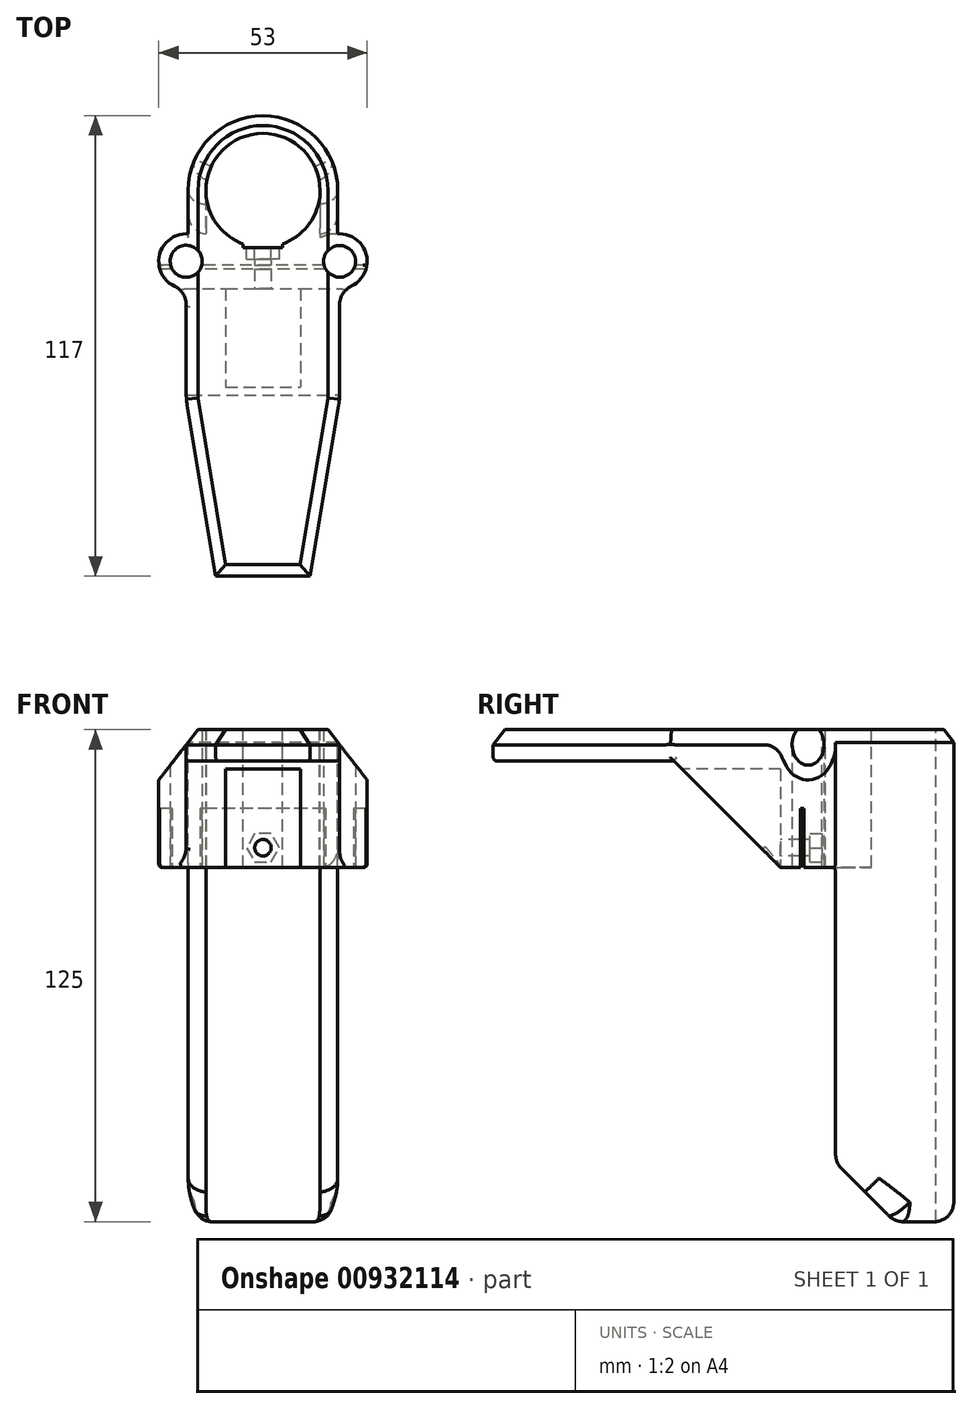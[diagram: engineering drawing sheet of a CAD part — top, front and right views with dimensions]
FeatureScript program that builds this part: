
annotation { "Feature Type Name" : "Feature", "Feature Type Description" : "" }
export const myFeature = defineFeature(function(context is Context, id is Id, definition is map)
    precondition{}
    {
        {
            var Q0;
            Q0=qCreatedBy(makeId("Top.planeOp"),FACE);
            var sketch = newSketch(context, id + "F0", { "sketchPlane" : qUnion([Q0])});
            skCircle(sketch, "E0", {"center": v(-19.5, 0) * mm, "radius": 4.08 * mm});
            skCircle(sketch, "E1", {"center": v(19.5, 0) * mm, "radius": 4.08 * mm});
            skLineSegment(sketch, "E2", {"start": v(0, 0) * mm, "end": v(-19.5, 0) * mm, "construction": true});
            skLineSegment(sketch, "E3", {"start": v(0, 0) * mm, "end": v(19.5, 0) * mm, "construction": true});
            skArc(sketch, "E4", {"start": v(-19.5, 7) * mm, "mid": v(-26.5, 0) * mm, "end": v(-19.5, -7) * mm});
            skArc(sketch, "E5", {"start": v(19.5, -7) * mm, "mid": v(26.5, 0) * mm, "end": v(19.5, 7) * mm});
            skLineSegment(sketch, "E6", {"start": v(-19.5, 7) * mm, "end": v(-19.5, 16.05) * mm});
            skLineSegment(sketch, "E7", {"start": v(-19.5, 16.05) * mm, "end": v(0, 16.05) * mm});
            skLineSegment(sketch, "E8.MirrorCS", {"start": v(19.5, 16.05) * mm, "end": v(0, 16.05) * mm});
            skLineSegment(sketch, "E9.MirrorCS", {"start": v(19.5, 7) * mm, "end": v(19.5, 16.05) * mm});
            skLineSegment(sketch, "E10", {"start": v(-19.5, 7) * mm, "end": v(-19.5, 0) * mm, "construction": true});
            skLineSegment(sketch, "E11", {"start": v(0, 16.05) * mm, "end": v(0, 16.05) * mm});
            skLineSegment(sketch, "E12", {"start": v(-19.5, -7) * mm, "end": v(-19.5, -35) * mm});
            skLineSegment(sketch, "E13", {"start": v(-19.5, -35) * mm, "end": v(-12, -80) * mm});
            skLineSegment(sketch, "E14", {"start": v(-12, -80) * mm, "end": v(0, -80) * mm});
            skLineSegment(sketch, "E15.MirrorCS", {"start": v(19.5, -7) * mm, "end": v(19.5, -35) * mm});
            skLineSegment(sketch, "E16.MirrorCS", {"start": v(12, -80) * mm, "end": v(0, -80) * mm});
            skLineSegment(sketch, "E17.MirrorCS", {"start": v(19.5, -35) * mm, "end": v(12, -80) * mm});
            skSolve(sketch);
        }
        {
            var Q0;
            Q0=makeQuery(id+"F0.imprint","IMPRINT",FACE,{"disambiguationData":[TD([[makeQuery(id+"F0.imprint","IMPRINT",EDGE,{"derivedFrom":sQuery(id+"F0.wireOp",EDGE,"E0")}),-1.0]])]});
            extrude(context, id + "F1", {"entities" : qUnion([Q0]), "depth" : 35 * mm, "offsetDistance" : 25 * mm});
        }
        {
            var Q0;
            Q0=makeQuery(id+"F1.opExtrude","SWEPT_FACE",FACE,{"disambiguationData":[OSD([sQuery(id+"F0.wireOp",EDGE,"E15.MirrorCS")])]});
            var sketch = newSketch(context, id + "F2", { "sketchPlane" : qUnion([Q0])});
            skLineSegment(sketch, "E18", {"start": v(-82.24, 27) * mm, "end": v(-34, 27) * mm});
            skLineSegment(sketch, "E19", {"start": v(-34, 27) * mm, "end": v(-7, 0) * mm});
            skLineSegment(sketch, "E20", {"start": v(-7, 0) * mm, "end": v(-7, 0) * mm});
            skLineSegment(sketch, "E21", {"start": v(-7, 0) * mm, "end": v(-7, -26.34) * mm});
            skLineSegment(sketch, "E22", {"start": v(-7, -26.34) * mm, "end": v(-82.24, -26.34) * mm});
            skLineSegment(sketch, "E23", {"start": v(-82.24, 27) * mm, "end": v(-82.24, -26.34) * mm});
            skSolve(sketch);
        }
        {
            var Q0;
            Q0=makeQuery(id+"F2.imprint","IMPRINT",FACE,{"disambiguationData":[TD([[makeQuery(id+"F2.imprint","IMPRINT",EDGE,{"derivedFrom":sQuery(id+"F2.wireOp",EDGE,"E21")}),-1.0]])]});
            var Q1;
            {var subQ0=sQuery(id+"F2.wireOp",EDGE,"E19");Q1=makeQuery(id+"F2.imprint","IMPRINT",FACE,{"disambiguationData":[TD([[makeQuery(id+"F2.imprint","IMPRINT",EDGE,{"derivedFrom":subQ0}),-1.0]])]});}
            extrude(context, id + "F3", {"entities" : qUnion([Q0, Q1]), "operationType" : NewBodyOperationType.REMOVE, "endBound" : BoundingType.THROUGH_ALL, "oppositeDirection" : true, "depth" : 25 * mm, "offsetDistance" : 25 * mm});
        }
        {
            var Q0;
            Q0=makeQuery(id+"F1.opExtrude","CAP_EDGE",EDGE,{"disambiguationData":[OSD([sQuery(id+"F0.wireOp",EDGE,"E13")])],"isStart":false});
            var Q1;
            Q1=makeQuery(id+"F1.opExtrude","CAP_EDGE",EDGE,{"disambiguationData":[OSD([sQuery(id+"F0.wireOp",EDGE,"E12")])],"isStart":false});
            var Q2;
            Q2=makeQuery(id+"F1.opExtrude","CAP_EDGE",EDGE,{"disambiguationData":[OSD([sQuery(id+"F0.wireOp",EDGE,"E15.MirrorCS")])],"isStart":false});
            var Q3;
            Q3=makeQuery(id+"F1.opExtrude","CAP_EDGE",EDGE,{"disambiguationData":[OSD([sQuery(id+"F0.wireOp",EDGE,"E9.MirrorCS")])],"isStart":false});
            var Q4;
            Q4=makeQuery(id+"F1.opExtrude","CAP_EDGE",EDGE,{"disambiguationData":[OSD([sQuery(id+"F0.wireOp",EDGE,"E6")])],"isStart":false});
            var Q5;
            Q5=makeQuery(id+"F1.opExtrude","CAP_EDGE",EDGE,{"disambiguationData":[OSD([sQuery(id+"F0.wireOp",EDGE,"E17.MirrorCS")])],"isStart":false});
            var Q6;
            Q6=makeQuery(id+"F1.opExtrude","CAP_EDGE",EDGE,{"disambiguationData":[OSD([sQuery(id+"F0.wireOp",EDGE,"E14"),sQuery(id+"F0.wireOp",EDGE,"E16.MirrorCS")])],"isStart":false});
            chamfer(context, id + "F4", {"entities" : qUnion([Q0, Q1, Q2, Q3, Q4, Q5, Q6]), "chamferType" : ChamferType.OFFSET_ANGLE, "width" : 3 * mm, "oppositeDirection" : false, "angle" : 52 * degree, "tangentPropagation" : true});
        }
        {
            var Q0;
            Q0=makeQuery(id+"F1.opExtrude","SWEPT_FACE",FACE,{"disambiguationData":[OSD([sQuery(id+"F0.wireOp",EDGE,"E14"),sQuery(id+"F0.wireOp",EDGE,"E16.MirrorCS")])]});
            var sketch = newSketch(context, id + "F5", { "sketchPlane" : qUnion([Q0])});
            skLineSegment(sketch, "E24", {"start": v(-16.5, 35) * mm, "end": v(-35.5, 10.68) * mm});
            skLineSegment(sketch, "E25", {"start": v(-35.5, 10.68) * mm, "end": v(-35.5, 37.22) * mm});
            skLineSegment(sketch, "E26", {"start": v(-35.5, 37.22) * mm, "end": v(0, 37.22) * mm});
            skLineSegment(sketch, "E27", {"start": v(0, 37.22) * mm, "end": v(0, 35) * mm});
            skLineSegment(sketch, "E28", {"start": v(0, 35) * mm, "end": v(-16.5, 35) * mm});
            skLineSegment(sketch, "E29.MirrorCS", {"start": v(0, 35) * mm, "end": v(16.5, 35) * mm});
            skLineSegment(sketch, "E30.MirrorCS", {"start": v(35.5, 37.22) * mm, "end": v(0, 37.22) * mm});
            skLineSegment(sketch, "E31.MirrorCS", {"start": v(35.5, 10.68) * mm, "end": v(35.5, 37.22) * mm});
            skLineSegment(sketch, "E32.MirrorCS", {"start": v(16.5, 35) * mm, "end": v(35.5, 10.68) * mm});
            skSolve(sketch);
        }
        {
            var Q0;
            Q0 = qSketchRegion(id + "F5", true);
            extrude(context, id + "F6", {"entities" : qUnion([Q0]), "operationType" : NewBodyOperationType.REMOVE, "endBound" : BoundingType.THROUGH_ALL, "oppositeDirection" : true, "depth" : 25 * mm, "offsetDistance" : 25 * mm});
        }
        {
            var Q0;
            Q0=makeQuery(id+"F1.opExtrude","CAP_FACE",FACE,{"disambiguationData":[OSD([sQuery(id+"F0.wireOp",EDGE,"E0"),sQuery(id+"F0.wireOp",EDGE,"E1"),sQuery(id+"F0.wireOp",EDGE,"E4"),sQuery(id+"F0.wireOp",EDGE,"E5"),sQuery(id+"F0.wireOp",EDGE,"E6"),sQuery(id+"F0.wireOp",EDGE,"E7"),sQuery(id+"F0.wireOp",EDGE,"E8.MirrorCS"),sQuery(id+"F0.wireOp",EDGE,"E9.MirrorCS"),sQuery(id+"F0.wireOp",EDGE,"4d2fa844-fc57-4d47-8dba-1bd83d5faa9b2.MirrorC"),sQuery(id+"F0.wireOp",EDGE,"E12"),sQuery(id+"F0.wireOp",EDGE,"E13"),sQuery(id+"F0.wireOp",EDGE,"E14"),sQuery(id+"F0.wireOp",EDGE,"E15.MirrorCS"),sQuery(id+"F0.wireOp",EDGE,"E16.MirrorCS"),sQuery(id+"F0.wireOp",EDGE,"E17.MirrorCS")])],"isStart":true});
            var sketch = newSketch(context, id + "F7", { "sketchPlane" : qUnion([Q0])});
            skLineSegment(sketch, "E33.bottom", {"start": v(96.32, 1) * mm, "end": v(-96.32, 1) * mm});
            skLineSegment(sketch, "E33.top", {"start": v(96.32, 2) * mm, "end": v(-96.32, 2) * mm});
            skLineSegment(sketch, "E33.left", {"start": v(96.32, 1) * mm, "end": v(96.32, 2) * mm});
            skLineSegment(sketch, "E33.right", {"start": v(-96.32, 1) * mm, "end": v(-96.32, 2) * mm});
            skPoint(sketch, "E33.middle", {"position": v(0, 1.5) * mm});
            skSolve(sketch);
        }
        {
            var Q0;
            Q0 = qSketchRegion(id + "F7", true);
            extrude(context, id + "F8", {"entities" : qUnion([Q0]), "operationType" : NewBodyOperationType.REMOVE, "oppositeDirection" : true, "depth" : 15 * mm, "offsetDistance" : 25 * mm});
        }
        {
            var Q0;
            {var subQ0=sQuery(id+"F0.wireOp",EDGE,"E4");var subQ1=sQuery(id+"F0.wireOp",EDGE,"E1");var subQ2=sQuery(id+"F0.wireOp",EDGE,"E15.MirrorCS");var subQ3=sQuery(id+"F0.wireOp",EDGE,"E5");var subQ4=sQuery(id+"F0.wireOp",EDGE,"E0");var subQ5=sQuery(id+"F0.wireOp",EDGE,"E12");Q0=makeQuery(id+"F8.boolean.opBoolean","SPLIT",FACE,{"disambiguationData":[TD([makeQuery(id+"F1.opExtrude","SWEPT_FACE",FACE,{"disambiguationData":[OSD([subQ5])]})])],"derivedFrom":makeQuery(id+"F1.opExtrude","CAP_FACE",FACE,{"disambiguationData":[OSD([subQ4,subQ1,subQ0,subQ3,sQuery(id+"F0.wireOp",EDGE,"E6"),sQuery(id+"F0.wireOp",EDGE,"E7"),sQuery(id+"F0.wireOp",EDGE,"E8.MirrorCS"),sQuery(id+"F0.wireOp",EDGE,"E9.MirrorCS"),sQuery(id+"F0.wireOp",EDGE,"4d2fa844-fc57-4d47-8dba-1bd83d5faa9b2.MirrorC"),subQ5,sQuery(id+"F0.wireOp",EDGE,"E13"),sQuery(id+"F0.wireOp",EDGE,"E14"),subQ2,sQuery(id+"F0.wireOp",EDGE,"E16.MirrorCS"),sQuery(id+"F0.wireOp",EDGE,"E17.MirrorCS")])],"isStart":true})});}
            var sketch = newSketch(context, id + "F9", { "sketchPlane" : qUnion([Q0])});
            skLineSegment(sketch, "E34.bottom", {"start": v(-3.75, 7) * mm, "end": v(3.75, 7) * mm});
            skLineSegment(sketch, "E34.top", {"start": v(-3.75, 17) * mm, "end": v(3.75, 17) * mm});
            skLineSegment(sketch, "E34.left", {"start": v(-3.75, 7) * mm, "end": v(-3.75, 17) * mm});
            skLineSegment(sketch, "E34.right", {"start": v(3.75, 7) * mm, "end": v(3.75, 17) * mm});
            skPoint(sketch, "E34.middle", {"position": v(0, 12) * mm});
            skPoint(sketch, "E34.middle.positionSnap0", {"position": v(0, 7) * mm});
            skPoint(sketch, "E34.centerSnap0", {"position": v(0, 7) * mm});
            skSolve(sketch);
        }
        {
            var Q0;
            Q0=makeQuery(id+"F9.imprint","IMPRINT",FACE,{"disambiguationData":[TD([[makeQuery(id+"F9.imprint","IMPRINT",EDGE,{"derivedFrom":sQuery(id+"F9.wireOp",EDGE,"E34.bottom")}),1.0]])]});
            extrude(context, id + "F10", {"entities" : qUnion([Q0]), "operationType" : NewBodyOperationType.REMOVE, "oppositeDirection" : true, "depth" : 10 * mm, "offsetDistance" : 25 * mm});
        }
        {
            var Q0;
            Q0=makeQuery(id+"F1.opExtrude","CAP_FACE",FACE,{"disambiguationData":[OSD([sQuery(id+"F0.wireOp",EDGE,"E0"),sQuery(id+"F0.wireOp",EDGE,"E1"),sQuery(id+"F0.wireOp",EDGE,"E4"),sQuery(id+"F0.wireOp",EDGE,"E5"),sQuery(id+"F0.wireOp",EDGE,"E6"),sQuery(id+"F0.wireOp",EDGE,"E7"),sQuery(id+"F0.wireOp",EDGE,"E8.MirrorCS"),sQuery(id+"F0.wireOp",EDGE,"E9.MirrorCS"),sQuery(id+"F0.wireOp",EDGE,"E12"),sQuery(id+"F0.wireOp",EDGE,"E13"),sQuery(id+"F0.wireOp",EDGE,"E14"),sQuery(id+"F0.wireOp",EDGE,"E15.MirrorCS"),sQuery(id+"F0.wireOp",EDGE,"E16.MirrorCS"),sQuery(id+"F0.wireOp",EDGE,"E17.MirrorCS")])],"isStart":false});
            var sketch = newSketch(context, id + "F11", { "sketchPlane" : qUnion([Q0])});
            skLineSegment(sketch, "E35.bottom", {"start": v(14.5, 16.05) * mm, "end": v(19.5, 16.05) * mm});
            skLineSegment(sketch, "E35.top", {"start": v(14.5, 7) * mm, "end": v(19.5, 7) * mm});
            skLineSegment(sketch, "E35.left", {"start": v(14.5, 16.05) * mm, "end": v(14.5, 7) * mm});
            skLineSegment(sketch, "E35.right", {"start": v(19.5, 16.05) * mm, "end": v(19.5, 7) * mm});
            skLineSegment(sketch, "E36.MirrorCS", {"start": v(-19.5, 16.05) * mm, "end": v(-19.5, 7) * mm});
            skLineSegment(sketch, "E37.MirrorCS", {"start": v(-14.5, 7) * mm, "end": v(-19.5, 7) * mm});
            skLineSegment(sketch, "E38.MirrorCS", {"start": v(-14.5, 16.05) * mm, "end": v(-14.5, 7) * mm});
            skLineSegment(sketch, "E39.MirrorCS", {"start": v(-14.5, 16.05) * mm, "end": v(-19.5, 16.05) * mm});
            skSolve(sketch);
        }
        {
            var Q0;
            Q0 = qSketchRegion(id + "F11", true);
            extrude(context, id + "F12", {"entities" : qUnion([Q0]), "operationType" : NewBodyOperationType.REMOVE, "endBound" : BoundingType.THROUGH_ALL, "oppositeDirection" : true, "depth" : 25 * mm, "offsetDistance" : 25 * mm});
        }
        {
            var Q0;
            Q0=makeQuery(id+"F10.boolean.opBoolean","COPY",FACE,{"derivedFrom":makeQuery(id+"F10.opExtrude","SWEPT_FACE",FACE,{"disambiguationData":[OSD([sQuery(id+"F9.wireOp",EDGE,"E34.bottom")])]})});
            var sketch = newSketch(context, id + "F13", { "sketchPlane" : qUnion([Q0])});
            skCircle(sketch, "E40", {"center": v(0, 5) * mm, "radius": 2.1 * mm});
            skSolve(sketch);
        }
        {
            var Q0;
            Q0 = qSketchRegion(id + "F13", true);
            extrude(context, id + "F14", {"entities" : qUnion([Q0]), "operationType" : NewBodyOperationType.REMOVE, "oppositeDirection" : true, "depth" : 25 * mm, "offsetDistance" : 25 * mm});
        }
        {
            var Q0;
            Q0=makeQuery(id+"F1.opExtrude","SWEPT_FACE",FACE,{"disambiguationData":[OSD([sQuery(id+"F0.wireOp",EDGE,"E7"),sQuery(id+"F0.wireOp",EDGE,"E8.MirrorCS")])]});
            var sketch = newSketch(context, id + "F15", { "sketchPlane" : qUnion([Q0])});
            skCircle(sketch, "E41.cCircle", {"center": v(0, 5) * mm, "radius": 3.6 * mm, "construction": true});
            skLineSegment(sketch, "E41.0", {"start": v(-4.16, 5) * mm, "end": v(-2.08, 8.6) * mm});
            skLineSegment(sketch, "E41.1", {"start": v(-2.08, 8.6) * mm, "end": v(2.08, 8.6) * mm});
            skLineSegment(sketch, "E41.2", {"start": v(2.08, 8.6) * mm, "end": v(4.16, 5) * mm});
            skLineSegment(sketch, "E41.3", {"start": v(4.16, 5) * mm, "end": v(2.08, 1.4) * mm});
            skLineSegment(sketch, "E41.4", {"start": v(2.08, 1.4) * mm, "end": v(-2.08, 1.4) * mm});
            skLineSegment(sketch, "E41.5", {"start": v(-2.08, 1.4) * mm, "end": v(-4.16, 5) * mm});
            skPoint(sketch, "E41.0.midPoint", {"position": v(-3.12, 6.8) * mm});
            skLineSegment(sketch, "E42", {"start": v(0, 5) * mm, "end": v(0, 0) * mm, "construction": true});
            skSolve(sketch);
        }
        {
            var Q0;
            Q0=makeQuery(id+"F15.imprint","IMPRINT",FACE,{"disambiguationData":[TD([[makeQuery(id+"F15.imprint","IMPRINT",EDGE,{"derivedFrom":sQuery(id+"F15.wireOp",EDGE,"E41.0")}),-1.0]])]});
            extrude(context, id + "F16", {"entities" : qUnion([Q0]), "operationType" : NewBodyOperationType.REMOVE, "oppositeDirection" : true, "depth" : 6 * mm, "offsetDistance" : 25 * mm});
        }
        {
            var Q0;
            {var subQ0=sQuery(id+"F0.wireOp",EDGE,"E4");var subQ1=sQuery(id+"F0.wireOp",EDGE,"E1");var subQ2=sQuery(id+"F0.wireOp",EDGE,"E5");var subQ3=sQuery(id+"F0.wireOp",EDGE,"E0");var subQ4=sQuery(id+"F0.wireOp",EDGE,"E12");var subQ5=sQuery(id+"F0.wireOp",EDGE,"E15.MirrorCS");Q0=makeQuery(id+"F8.boolean.opBoolean","SPLIT",FACE,{"disambiguationData":[TD([makeQuery(id+"F1.opExtrude","SWEPT_FACE",FACE,{"disambiguationData":[OSD([subQ4])]})])],"derivedFrom":makeQuery(id+"F1.opExtrude","CAP_FACE",FACE,{"disambiguationData":[OSD([subQ3,subQ1,subQ0,subQ2,sQuery(id+"F0.wireOp",EDGE,"E6"),sQuery(id+"F0.wireOp",EDGE,"E7"),sQuery(id+"F0.wireOp",EDGE,"E8.MirrorCS"),sQuery(id+"F0.wireOp",EDGE,"E9.MirrorCS"),subQ4,sQuery(id+"F0.wireOp",EDGE,"E13"),sQuery(id+"F0.wireOp",EDGE,"E14"),subQ5,sQuery(id+"F0.wireOp",EDGE,"E16.MirrorCS"),sQuery(id+"F0.wireOp",EDGE,"E17.MirrorCS")])],"isStart":true})});}
            var sketch = newSketch(context, id + "F17", { "sketchPlane" : qUnion([Q0])});
            skLineSegment(sketch, "E43.bottom", {"start": v(-9.5, 7) * mm, "end": v(9.5, 7) * mm});
            skLineSegment(sketch, "E43.top", {"start": v(-9.5, 43.79) * mm, "end": v(9.5, 43.79) * mm});
            skLineSegment(sketch, "E43.left", {"start": v(-9.5, 7) * mm, "end": v(-9.5, 43.79) * mm});
            skLineSegment(sketch, "E43.right", {"start": v(9.5, 7) * mm, "end": v(9.5, 43.79) * mm});
            skSolve(sketch);
        }
        {
            var Q0;
            Q0=makeQuery(id+"F17.imprint","IMPRINT",FACE,{"disambiguationData":[TD([[makeQuery(id+"F17.imprint","IMPRINT",EDGE,{"derivedFrom":sQuery(id+"F17.wireOp",EDGE,"E43.top")}),-1.0]])]});
            extrude(context, id + "F18", {"entities" : qUnion([Q0]), "operationType" : NewBodyOperationType.REMOVE, "oppositeDirection" : true, "depth" : 25 * mm, "offsetDistance" : 25 * mm});
        }
        {
            var Q0;
            Q0=makeQuery(id+"F1.opExtrude","SWEPT_EDGE",EDGE,{"disambiguationData":[OSD([sQuery(id+"F0.wireOp",EDGE,"E4"),sQuery(id+"F0.wireOp",EDGE,"E12")])]});
            var Q1;
            Q1=makeQuery(id+"F1.opExtrude","SWEPT_EDGE",EDGE,{"disambiguationData":[OSD([sQuery(id+"F0.wireOp",EDGE,"E5"),sQuery(id+"F0.wireOp",EDGE,"E15.MirrorCS")])]});
            fillet(context, id + "F19", {"entities" : qUnion([Q0, Q1]), "radius" : 5 * mm, "tangentPropagation" : true, "allowEdgeOverflow" : false});
        }
        {
            var Q0;
            Q0=makeQuery(id+"F1.opExtrude","SWEPT_EDGE",EDGE,{"disambiguationData":[OSD([sQuery(id+"F0.wireOp",EDGE,"E12"),sQuery(id+"F0.wireOp",EDGE,"E13")])]});
            var Q1;
            Q1=makeQuery(id+"F1.opExtrude","SWEPT_EDGE",EDGE,{"disambiguationData":[OSD([sQuery(id+"F0.wireOp",EDGE,"E15.MirrorCS"),sQuery(id+"F0.wireOp",EDGE,"E17.MirrorCS")])]});
            fillet(context, id + "F20", {"entities" : qUnion([Q0, Q1]), "radius" : 20 * mm, "tangentPropagation" : true, "allowEdgeOverflow" : false});
        }
        {
            var Q0;
            Q0=makeQuery(id+"F1.opExtrude","CAP_FACE",FACE,{"disambiguationData":[OSD([sQuery(id+"F0.wireOp",EDGE,"E0"),sQuery(id+"F0.wireOp",EDGE,"E1"),sQuery(id+"F0.wireOp",EDGE,"E4"),sQuery(id+"F0.wireOp",EDGE,"E5"),sQuery(id+"F0.wireOp",EDGE,"E6"),sQuery(id+"F0.wireOp",EDGE,"E7"),sQuery(id+"F0.wireOp",EDGE,"E8.MirrorCS"),sQuery(id+"F0.wireOp",EDGE,"E9.MirrorCS"),sQuery(id+"F0.wireOp",EDGE,"E12"),sQuery(id+"F0.wireOp",EDGE,"E13"),sQuery(id+"F0.wireOp",EDGE,"E14"),sQuery(id+"F0.wireOp",EDGE,"E15.MirrorCS"),sQuery(id+"F0.wireOp",EDGE,"E16.MirrorCS"),sQuery(id+"F0.wireOp",EDGE,"E17.MirrorCS")])],"isStart":false});
            var sketch = newSketch(context, id + "F21", { "sketchPlane" : qUnion([Q0])});
            skLineSegment(sketch, "E44", {"start": v(-14.5, 18) * mm, "end": v(-14.5, 18) * mm});
            skArc(sketch, "E45", {"start": v(19, 18) * mm, "mid": v(0, 37) * mm, "end": v(-19, 18) * mm});
            skLineSegment(sketch, "E46", {"start": v(-19, 18) * mm, "end": v(-19, 7) * mm});
            skLineSegment(sketch, "E47", {"start": v(-19, 7) * mm, "end": v(-14.5, 7) * mm});
            skLineSegment(sketch, "E48", {"start": v(-14.5, 7) * mm, "end": v(-14.5, 18) * mm});
            skArc(sketch, "E49", {"start": v(14.5, 18) * mm, "mid": v(0, 32.5) * mm, "end": v(-14.5, 18) * mm});
            skLineSegment(sketch, "E50.MirrorCS", {"start": v(19, 18) * mm, "end": v(19, 7) * mm});
            skLineSegment(sketch, "E51.MirrorCS", {"start": v(14.5, 7) * mm, "end": v(14.5, 18) * mm});
            skLineSegment(sketch, "E52", {"start": v(0, 18) * mm, "end": v(0, 0) * mm, "construction": true});
            skLineSegment(sketch, "E53", {"start": v(14.5, 7) * mm, "end": v(19, 7) * mm});
            skSolve(sketch);
        }
        {
            var Q0;
            Q0=makeQuery(id+"F21.imprint","IMPRINT",FACE,{"disambiguationData":[TD([[makeQuery(id+"F21.imprint","IMPRINT",EDGE,{"derivedFrom":sQuery(id+"F21.wireOp",EDGE,"E45")}),1.0]])]});
            extrude(context, id + "F22", {"entities" : qUnion([Q0]), "operationType" : NewBodyOperationType.ADD, "oppositeDirection" : true, "depth" : 125 * mm, "offsetDistance" : 25 * mm});
        }
        {
            var Q0;
            Q0=makeQuery(id+"F22.opExtrude","CAP_EDGE",EDGE,{"disambiguationData":[OSD([sQuery(id+"F21.wireOp",EDGE,"E46")])],"isStart":true});
            var Q1;
            Q1=makeQuery(id+"F22.opExtrude","CAP_EDGE",EDGE,{"disambiguationData":[OSD([sQuery(id+"F21.wireOp",EDGE,"E45")])],"isStart":true});
            var Q2;
            Q2=makeQuery(id+"F22.opExtrude","CAP_EDGE",EDGE,{"disambiguationData":[OSD([sQuery(id+"F21.wireOp",EDGE,"E50.MirrorCS")])],"isStart":true});
            chamfer(context, id + "F23", {"entities" : qUnion([Q0, Q1, Q2]), "chamferType" : ChamferType.OFFSET_ANGLE, "width" : 2.5 * mm, "oppositeDirection" : false, "angle" : 52 * degree, "tangentPropagation" : true});
        }
        {
            var Q0;
            Q0=makeQuery(id+"F22.boolean.opBoolean","MERGE",FACE,{"derivedFrom":[makeQuery(id+"F1.opExtrude","CAP_FACE",FACE,{"disambiguationData":[OSD([sQuery(id+"F0.wireOp",EDGE,"E0"),sQuery(id+"F0.wireOp",EDGE,"E1"),sQuery(id+"F0.wireOp",EDGE,"E4"),sQuery(id+"F0.wireOp",EDGE,"E5"),sQuery(id+"F0.wireOp",EDGE,"E6"),sQuery(id+"F0.wireOp",EDGE,"E7"),sQuery(id+"F0.wireOp",EDGE,"E8.MirrorCS"),sQuery(id+"F0.wireOp",EDGE,"E9.MirrorCS"),sQuery(id+"F0.wireOp",EDGE,"E12"),sQuery(id+"F0.wireOp",EDGE,"E13"),sQuery(id+"F0.wireOp",EDGE,"E14"),sQuery(id+"F0.wireOp",EDGE,"E15.MirrorCS"),sQuery(id+"F0.wireOp",EDGE,"E16.MirrorCS"),sQuery(id+"F0.wireOp",EDGE,"E17.MirrorCS")])],"isStart":false}),makeQuery(id+"F22.opExtrude","CAP_FACE",FACE,{"disambiguationData":[OSD([sQuery(id+"F21.wireOp",EDGE,"E45"),sQuery(id+"F21.wireOp",EDGE,"E46"),sQuery(id+"F21.wireOp",EDGE,"E47"),sQuery(id+"F21.wireOp",EDGE,"E48"),sQuery(id+"F21.wireOp",EDGE,"E49"),sQuery(id+"F21.wireOp",EDGE,"E50.MirrorCS"),sQuery(id+"F21.wireOp",EDGE,"E51.MirrorCS"),sQuery(id+"F21.wireOp",EDGE,"E53")])],"isStart":true})]});
            var sketch = newSketch(context, id + "F24", { "sketchPlane" : qUnion([Q0])});
            skArc(sketch, "E54", {"start": v(5, 4.39) * mm, "mid": v(0, 32.5) * mm, "end": v(-5, 4.39) * mm});
            skLineSegment(sketch, "E55.bottom", {"start": v(-5, 3.5) * mm, "end": v(5, 3.5) * mm});
            skLineSegment(sketch, "E55.left", {"start": v(-5, 3.5) * mm, "end": v(-5, 4.39) * mm});
            skLineSegment(sketch, "E55.right", {"start": v(5, 3.5) * mm, "end": v(5, 4.39) * mm});
            skPoint(sketch, "E55.middle", {"position": v(0, 5.46) * mm});
            skPoint(sketch, "E55.top.end.orphan", {"position": v(5, 7.42) * mm});
            skPoint(sketch, "E55.top.start.orphan", {"position": v(-5, 7.42) * mm});
            skSolve(sketch);
        }
        {
            var Q0;
            Q0 = qSketchRegion(id + "F24", true);
            extrude(context, id + "F25", {"entities" : qUnion([Q0]), "operationType" : NewBodyOperationType.REMOVE, "endBound" : BoundingType.THROUGH_ALL, "oppositeDirection" : true, "depth" : 25 * mm, "offsetDistance" : 25 * mm});
        }
        {
            var Q0;
            Q0=makeQuery(id+"F3.boolean.opBoolean","INTERSECT",EDGE,{"derivedFrom":[makeQuery(id+"F1.opExtrude","SWEPT_FACE",FACE,{"disambiguationData":[OSD([sQuery(id+"F0.wireOp",EDGE,"E17.MirrorCS")])]}),makeQuery(id+"F3.opExtrude","SWEPT_FACE",FACE,{"disambiguationData":[OSD([sQuery(id+"F2.wireOp",EDGE,"E18")])]})]});
            var Q1;
            Q1=makeQuery(id+"F3.boolean.opBoolean","INTERSECT",EDGE,{"derivedFrom":[makeQuery(id+"F1.opExtrude","SWEPT_FACE",FACE,{"disambiguationData":[OSD([sQuery(id+"F0.wireOp",EDGE,"E14"),sQuery(id+"F0.wireOp",EDGE,"E16.MirrorCS")])]}),makeQuery(id+"F3.opExtrude","SWEPT_FACE",FACE,{"disambiguationData":[OSD([sQuery(id+"F2.wireOp",EDGE,"E18")])]})]});
            var Q2;
            Q2=makeQuery(id+"F3.boolean.opBoolean","INTERSECT",EDGE,{"derivedFrom":[makeQuery(id+"F1.opExtrude","SWEPT_FACE",FACE,{"disambiguationData":[OSD([sQuery(id+"F0.wireOp",EDGE,"E13")])]}),makeQuery(id+"F3.opExtrude","SWEPT_FACE",FACE,{"disambiguationData":[OSD([sQuery(id+"F2.wireOp",EDGE,"E18")])]})]});
            var Q3;
            Q3=makeQuery(id+"F3.boolean.opBoolean","INTERSECT",EDGE,{"derivedFrom":[makeQuery(id+"F1.opExtrude","SWEPT_FACE",FACE,{"disambiguationData":[OSD([sQuery(id+"F0.wireOp",EDGE,"E12")])]}),makeQuery(id+"F3.opExtrude","SWEPT_FACE",FACE,{"disambiguationData":[OSD([sQuery(id+"F2.wireOp",EDGE,"E19")])]})]});
            var Q4;
            Q4=makeQuery(id+"F3.boolean.opBoolean","COPY",EDGE,{"derivedFrom":makeQuery(id+"F3.opExtrude","CAP_EDGE",EDGE,{"disambiguationData":[OSD([sQuery(id+"F2.wireOp",EDGE,"E19")])],"isStart":true})});
            var Q5;
            {var subQ0=sQuery(id+"F0.wireOp",EDGE,"E15.MirrorCS");var subQ1=sQuery(id+"F0.wireOp",EDGE,"E5");Q5=makeQuery(id+"F8.boolean.opBoolean","SPLIT",EDGE,{"disambiguationData":[TD([makeQuery(id+"F1.opExtrude","SWEPT_FACE",FACE,{"disambiguationData":[OSD([subQ0])]})])],"derivedFrom":makeQuery(id+"F1.opExtrude","CAP_EDGE",EDGE,{"disambiguationData":[OSD([subQ1])],"isStart":true})});}
            var Q6;
            {var subQ0=sQuery(id+"F0.wireOp",EDGE,"E9.MirrorCS");var subQ1=sQuery(id+"F0.wireOp",EDGE,"E5");Q6=makeQuery(id+"F8.boolean.opBoolean","SPLIT",EDGE,{"disambiguationData":[TD([makeQuery(id+"F1.opExtrude","SWEPT_FACE",FACE,{"disambiguationData":[OSD([subQ0])]})])],"derivedFrom":makeQuery(id+"F1.opExtrude","CAP_EDGE",EDGE,{"disambiguationData":[OSD([subQ1])],"isStart":true})});}
            var Q7;
            {var subQ0=sQuery(id+"F0.wireOp",EDGE,"E12");var subQ1=sQuery(id+"F0.wireOp",EDGE,"E4");Q7=makeQuery(id+"F8.boolean.opBoolean","SPLIT",EDGE,{"disambiguationData":[TD([makeQuery(id+"F1.opExtrude","SWEPT_FACE",FACE,{"disambiguationData":[OSD([subQ0])]})])],"derivedFrom":makeQuery(id+"F1.opExtrude","CAP_EDGE",EDGE,{"disambiguationData":[OSD([subQ1])],"isStart":true})});}
            var Q8;
            {var subQ0=sQuery(id+"F0.wireOp",EDGE,"E6");var subQ1=sQuery(id+"F0.wireOp",EDGE,"E4");Q8=makeQuery(id+"F8.boolean.opBoolean","SPLIT",EDGE,{"disambiguationData":[TD([makeQuery(id+"F1.opExtrude","SWEPT_FACE",FACE,{"disambiguationData":[OSD([subQ0])]})])],"derivedFrom":makeQuery(id+"F1.opExtrude","CAP_EDGE",EDGE,{"disambiguationData":[OSD([subQ1])],"isStart":true})});}
            fillet(context, id + "F26", {"entities" : qUnion([Q0, Q1, Q2, Q3, Q4, Q5, Q6, Q7, Q8]), "radius" : 1 * mm, "tangentPropagation" : true, "allowEdgeOverflow" : false});
        }
        {
            var Q0;
            Q0=makeQuery(id+"F22.opExtrude","CAP_EDGE",EDGE,{"disambiguationData":[OSD([sQuery(id+"F21.wireOp",EDGE,"E53")])],"isStart":false});
            var Q1;
            Q1=makeQuery(id+"F22.opExtrude","CAP_EDGE",EDGE,{"disambiguationData":[OSD([sQuery(id+"F21.wireOp",EDGE,"E47")])],"isStart":false});
            chamfer(context, id + "F27", {"entities" : qUnion([Q0, Q1]), "width" : 15 * mm, "tangentPropagation" : true});
        }
        {
            var Q0;
            {var subQ0=sQuery(id+"F21.wireOp",EDGE,"E53");Q0=makeQuery(id+"F27.opChamfer","BLEND_EDGE",EDGE,{"blendedFrom":[makeQuery(id+"F22.opExtrude","CAP_EDGE",EDGE,{"disambiguationData":[OSD([subQ0])],"isStart":false}),makeQuery(id+"F22.opExtrude","CAP_FACE",FACE,{"disambiguationData":[OSD([sQuery(id+"F21.wireOp",EDGE,"E45"),sQuery(id+"F21.wireOp",EDGE,"E46"),sQuery(id+"F21.wireOp",EDGE,"E47"),sQuery(id+"F21.wireOp",EDGE,"E48"),sQuery(id+"F21.wireOp",EDGE,"E49"),sQuery(id+"F21.wireOp",EDGE,"E50.MirrorCS"),sQuery(id+"F21.wireOp",EDGE,"E51.MirrorCS"),subQ0])],"isStart":false})],"blendedInto":[makeQuery(id+"F22.opExtrude","CAP_FACE",FACE,{"disambiguationData":[OSD([sQuery(id+"F21.wireOp",EDGE,"E45"),sQuery(id+"F21.wireOp",EDGE,"E46"),sQuery(id+"F21.wireOp",EDGE,"E47"),sQuery(id+"F21.wireOp",EDGE,"E48"),sQuery(id+"F21.wireOp",EDGE,"E49"),sQuery(id+"F21.wireOp",EDGE,"E50.MirrorCS"),sQuery(id+"F21.wireOp",EDGE,"E51.MirrorCS"),subQ0])],"isStart":false})]});}
            var Q1;
            {var subQ0=sQuery(id+"F21.wireOp",EDGE,"E47");Q1=makeQuery(id+"F27.opChamfer","BLEND_EDGE",EDGE,{"blendedFrom":[makeQuery(id+"F22.opExtrude","CAP_EDGE",EDGE,{"disambiguationData":[OSD([subQ0])],"isStart":false}),makeQuery(id+"F22.opExtrude","CAP_FACE",FACE,{"disambiguationData":[OSD([sQuery(id+"F21.wireOp",EDGE,"E45"),sQuery(id+"F21.wireOp",EDGE,"E46"),subQ0,sQuery(id+"F21.wireOp",EDGE,"E48"),sQuery(id+"F21.wireOp",EDGE,"E49"),sQuery(id+"F21.wireOp",EDGE,"E50.MirrorCS"),sQuery(id+"F21.wireOp",EDGE,"E51.MirrorCS"),sQuery(id+"F21.wireOp",EDGE,"E53")])],"isStart":false})],"blendedInto":[makeQuery(id+"F22.opExtrude","CAP_FACE",FACE,{"disambiguationData":[OSD([sQuery(id+"F21.wireOp",EDGE,"E45"),sQuery(id+"F21.wireOp",EDGE,"E46"),subQ0,sQuery(id+"F21.wireOp",EDGE,"E48"),sQuery(id+"F21.wireOp",EDGE,"E49"),sQuery(id+"F21.wireOp",EDGE,"E50.MirrorCS"),sQuery(id+"F21.wireOp",EDGE,"E51.MirrorCS"),sQuery(id+"F21.wireOp",EDGE,"E53")])],"isStart":false})]});}
            var Q2;
            {var subQ1=sQuery(id+"F21.wireOp",EDGE,"E53");var subQ2=sQuery(id+"F21.wireOp",EDGE,"E51.MirrorCS");Q2=makeQuery(id+"F27.opChamfer","BLEND_EDGE",EDGE,{"blendedFrom":[makeQuery(id+"F22.opExtrude","CAP_EDGE",EDGE,{"disambiguationData":[OSD([subQ1])],"isStart":false}),makeQuery(id+"F22.boolean.opBoolean","SPLIT",FACE,{"disambiguationData":[TD([makeQuery(id+"F22.opExtrude","SWEPT_FACE",FACE,{"disambiguationData":[OSD([subQ2])]})])],"derivedFrom":makeQuery(id+"F22.opExtrude","SWEPT_FACE",FACE,{"disambiguationData":[OSD([subQ1])]})})],"blendedInto":[makeQuery(id+"F22.boolean.opBoolean","SPLIT",FACE,{"disambiguationData":[TD([makeQuery(id+"F22.opExtrude","SWEPT_FACE",FACE,{"disambiguationData":[OSD([subQ2])]})])],"derivedFrom":makeQuery(id+"F22.opExtrude","SWEPT_FACE",FACE,{"disambiguationData":[OSD([subQ1])]})})]});}
            var Q3;
            {var subQ0=sQuery(id+"F21.wireOp",EDGE,"E48");var subQ1=sQuery(id+"F21.wireOp",EDGE,"E47");Q3=makeQuery(id+"F27.opChamfer","BLEND_EDGE",EDGE,{"blendedFrom":[makeQuery(id+"F22.opExtrude","CAP_EDGE",EDGE,{"disambiguationData":[OSD([subQ1])],"isStart":false}),makeQuery(id+"F22.boolean.opBoolean","SPLIT",FACE,{"disambiguationData":[TD([makeQuery(id+"F22.opExtrude","SWEPT_FACE",FACE,{"disambiguationData":[OSD([subQ0])]})])],"derivedFrom":makeQuery(id+"F22.opExtrude","SWEPT_FACE",FACE,{"disambiguationData":[OSD([subQ1])]})})],"blendedInto":[makeQuery(id+"F22.boolean.opBoolean","SPLIT",FACE,{"disambiguationData":[TD([makeQuery(id+"F22.opExtrude","SWEPT_FACE",FACE,{"disambiguationData":[OSD([subQ0])]})])],"derivedFrom":makeQuery(id+"F22.opExtrude","SWEPT_FACE",FACE,{"disambiguationData":[OSD([subQ1])]})})]});}
            fillet(context, id + "F28", {"entities" : qUnion([Q0, Q1, Q2, Q3]), "radius" : 5 * mm, "tangentPropagation" : true, "allowEdgeOverflow" : false});
        }
        {
            var Q0;
            {var subQ0=sQuery(id+"F0.wireOp",EDGE,"E9.MirrorCS");var subQ1=sQuery(id+"F0.wireOp",EDGE,"E8.MirrorCS");var subQ2=sQuery(id+"F0.wireOp",EDGE,"E7");var subQ3=sQuery(id+"F0.wireOp",EDGE,"E6");var subQ4=sQuery(id+"F0.wireOp",EDGE,"E5");var subQ5=sQuery(id+"F0.wireOp",EDGE,"E4");var subQ6=sQuery(id+"F0.wireOp",EDGE,"E1");var subQ7=sQuery(id+"F0.wireOp",EDGE,"E0");var subQ8=makeQuery(id+"F1.opExtrude","CAP_FACE",FACE,{"disambiguationData":[OSD([subQ7,subQ6,subQ5,subQ4,subQ3,subQ2,subQ1,subQ0,sQuery(id+"F0.wireOp",EDGE,"E12"),sQuery(id+"F0.wireOp",EDGE,"E13"),sQuery(id+"F0.wireOp",EDGE,"E14"),sQuery(id+"F0.wireOp",EDGE,"E15.MirrorCS"),sQuery(id+"F0.wireOp",EDGE,"E16.MirrorCS"),sQuery(id+"F0.wireOp",EDGE,"E17.MirrorCS")])],"isStart":true});Q0=makeQuery(id+"F22.boolean.opBoolean","SPLIT",EDGE,{"disambiguationData":[topologyDisambiguationEdgeConnected([makeQuery(id+"F22.opExtrude","SWEPT_FACE",FACE,{"disambiguationData":[OSD([sQuery(id+"F21.wireOp",EDGE,"E53")])]})])],"derivedFrom":makeQuery(id+"F12.boolean.opBoolean","INTERSECT",EDGE,{"derivedFrom":[makeQuery(id+"F8.boolean.opBoolean","SPLIT",FACE,{"disambiguationData":[TD([makeQuery(id+"F1.opExtrude","SWEPT_FACE",FACE,{"disambiguationData":[OSD([subQ3])]})])],"derivedFrom":subQ8}),makeQuery(id+"F12.opExtrude","SWEPT_FACE",FACE,{"disambiguationData":[OSD([sQuery(id+"F11.wireOp",EDGE,"E35.top")])]})]})});}
            var Q1;
            {var subQ0=sQuery(id+"F0.wireOp",EDGE,"E9.MirrorCS");var subQ1=sQuery(id+"F0.wireOp",EDGE,"E8.MirrorCS");var subQ2=sQuery(id+"F0.wireOp",EDGE,"E7");var subQ3=sQuery(id+"F0.wireOp",EDGE,"E6");var subQ4=sQuery(id+"F0.wireOp",EDGE,"E5");var subQ5=sQuery(id+"F0.wireOp",EDGE,"E4");var subQ6=sQuery(id+"F0.wireOp",EDGE,"E1");var subQ7=sQuery(id+"F0.wireOp",EDGE,"E0");var subQ8=makeQuery(id+"F1.opExtrude","CAP_FACE",FACE,{"disambiguationData":[OSD([subQ7,subQ6,subQ5,subQ4,subQ3,subQ2,subQ1,subQ0,sQuery(id+"F0.wireOp",EDGE,"E12"),sQuery(id+"F0.wireOp",EDGE,"E13"),sQuery(id+"F0.wireOp",EDGE,"E14"),sQuery(id+"F0.wireOp",EDGE,"E15.MirrorCS"),sQuery(id+"F0.wireOp",EDGE,"E16.MirrorCS"),sQuery(id+"F0.wireOp",EDGE,"E17.MirrorCS")])],"isStart":true});Q1=makeQuery(id+"F22.boolean.opBoolean","SPLIT",EDGE,{"disambiguationData":[topologyDisambiguationEdgeConnected([makeQuery(id+"F22.opExtrude","SWEPT_FACE",FACE,{"disambiguationData":[OSD([sQuery(id+"F21.wireOp",EDGE,"E47")])]})])],"derivedFrom":makeQuery(id+"F12.boolean.opBoolean","INTERSECT",EDGE,{"derivedFrom":[makeQuery(id+"F8.boolean.opBoolean","SPLIT",FACE,{"disambiguationData":[TD([makeQuery(id+"F1.opExtrude","SWEPT_FACE",FACE,{"disambiguationData":[OSD([subQ3])]})])],"derivedFrom":subQ8}),makeQuery(id+"F12.opExtrude","SWEPT_FACE",FACE,{"disambiguationData":[OSD([sQuery(id+"F11.wireOp",EDGE,"E37.MirrorCS")])]})]})});}
            fillet(context, id + "F29", {"entities" : qUnion([Q0, Q1]), "radius" : 1 * mm, "tangentPropagation" : true, "allowEdgeOverflow" : false});
        }
        {
            var Q0;
            {var subQ0=sQuery(id+"F21.wireOp",EDGE,"E50.MirrorCS");Q0=makeQuery(id+"F22.boolean.opBoolean","SPLIT",EDGE,{"disambiguationData":[topologyDisambiguationEdgeConnected([makeQuery(id+"F12.boolean.opBoolean","COPY",FACE,{"derivedFrom":makeQuery(id+"F12.opExtrude","SWEPT_FACE",FACE,{"disambiguationData":[OSD([sQuery(id+"F11.wireOp",EDGE,"E35.top")])]})}),makeQuery(id+"F22.opExtrude","SWEPT_FACE",FACE,{"disambiguationData":[OSD([subQ0])]})])],"derivedFrom":makeQuery(id+"F22.opExtrude","SWEPT_EDGE",EDGE,{"disambiguationData":[OSD([subQ0,sQuery(id+"F21.wireOp",EDGE,"E53")])]})});}
            var Q1;
            {var subQ0=sQuery(id+"F21.wireOp",EDGE,"E46");Q1=makeQuery(id+"F22.boolean.opBoolean","SPLIT",EDGE,{"disambiguationData":[topologyDisambiguationEdgeConnected([makeQuery(id+"F12.boolean.opBoolean","COPY",FACE,{"derivedFrom":makeQuery(id+"F12.opExtrude","SWEPT_FACE",FACE,{"disambiguationData":[OSD([sQuery(id+"F11.wireOp",EDGE,"E37.MirrorCS")])]})}),makeQuery(id+"F22.opExtrude","SWEPT_FACE",FACE,{"disambiguationData":[OSD([subQ0])]})])],"derivedFrom":makeQuery(id+"F22.opExtrude","SWEPT_EDGE",EDGE,{"disambiguationData":[OSD([subQ0,sQuery(id+"F21.wireOp",EDGE,"E47")])]})});}
            fillet(context, id + "F30", {"entities" : qUnion([Q0, Q1]), "radius" : 5 * mm, "tangentPropagation" : true, "allowEdgeOverflow" : false});
        }
        {
            var Q0;
            Q0=makeQuery(id+"F25.boolean.opBoolean","COPY",FACE,{"derivedFrom":makeQuery(id+"F25.opExtrude","SWEPT_FACE",FACE,{"disambiguationData":[OSD([sQuery(id+"F24.wireOp",EDGE,"E55.bottom")])]})});
            var sketch = newSketch(context, id + "F31", { "sketchPlane" : qUnion([Q0])});
            skCircle(sketch, "E56.cCircle", {"center": v(0, 5) * mm, "radius": 3.6 * mm, "construction": true});
            skLineSegment(sketch, "E56.0", {"start": v(-2.08, 8.6) * mm, "end": v(2.08, 8.6) * mm});
            skLineSegment(sketch, "E56.1", {"start": v(2.08, 8.6) * mm, "end": v(4.16, 5) * mm});
            skLineSegment(sketch, "E56.2", {"start": v(4.16, 5) * mm, "end": v(2.08, 1.4) * mm});
            skLineSegment(sketch, "E56.3", {"start": v(2.08, 1.4) * mm, "end": v(-2.08, 1.4) * mm});
            skLineSegment(sketch, "E56.4", {"start": v(-2.08, 1.4) * mm, "end": v(-4.16, 5) * mm});
            skLineSegment(sketch, "E56.5", {"start": v(-4.16, 5) * mm, "end": v(-2.08, 8.6) * mm});
            skPoint(sketch, "E56.0.midPoint", {"position": v(0, 8.6) * mm});
            skSolve(sketch);
        }
        {
            var Q0;
            Q0=makeQuery(id+"F31.imprint","IMPRINT",FACE,{"disambiguationData":[TD([[makeQuery(id+"F31.imprint","IMPRINT",EDGE,{"derivedFrom":sQuery(id+"F31.wireOp",EDGE,"E56.0")}),-1.0]])]});
            extrude(context, id + "F32", {"entities" : qUnion([Q0]), "operationType" : NewBodyOperationType.REMOVE, "oppositeDirection" : true, "depth" : 3 * mm, "offsetDistance" : 25 * mm});
        }
    });
